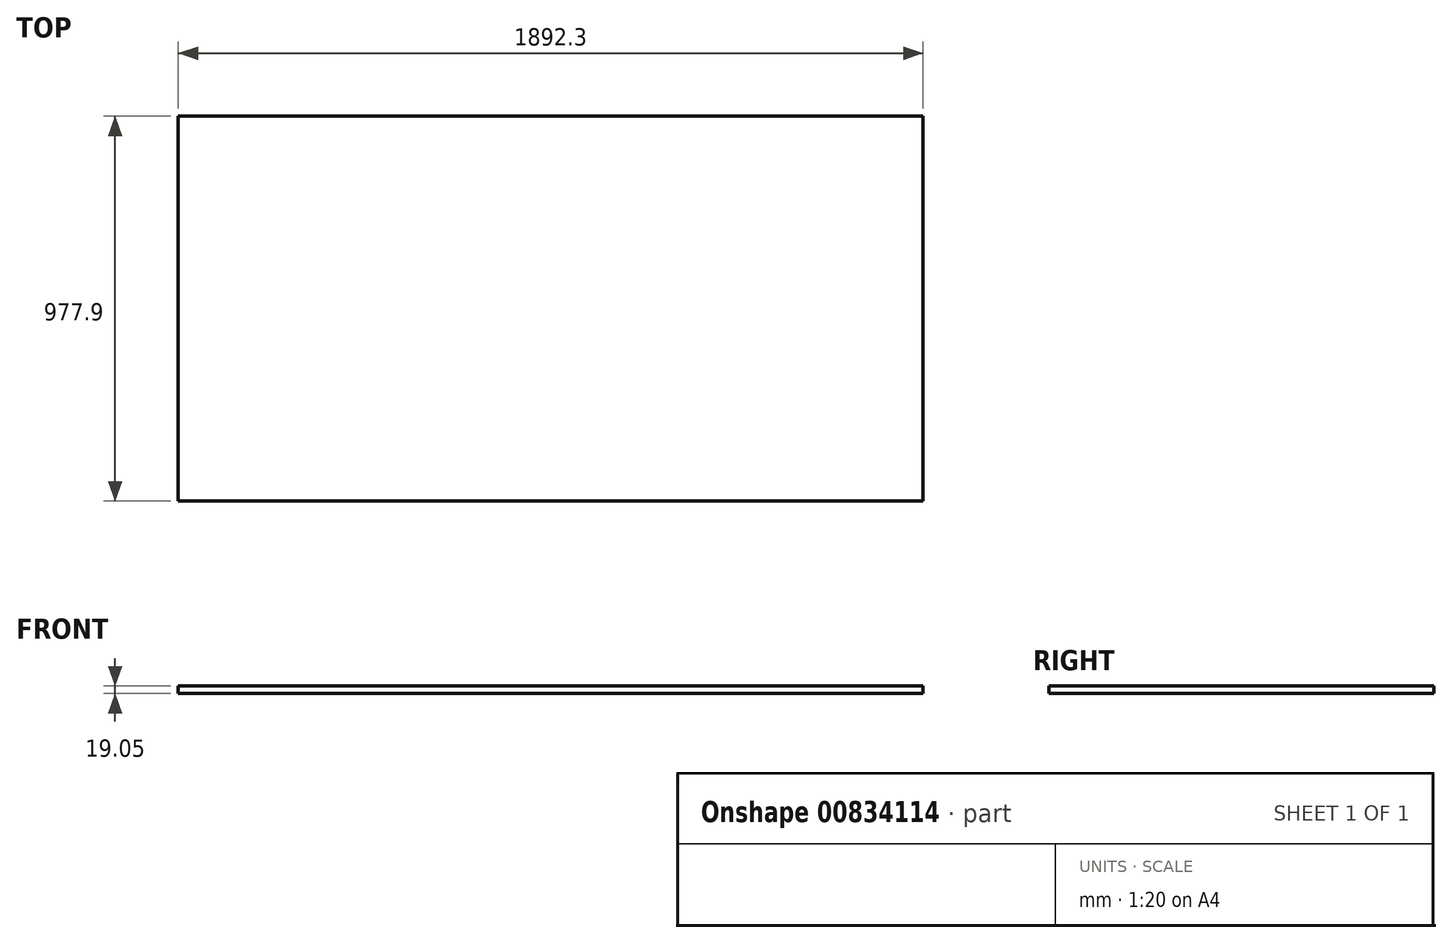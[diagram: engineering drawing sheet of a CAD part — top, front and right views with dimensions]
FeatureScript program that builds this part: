
annotation { "Feature Type Name" : "Feature", "Feature Type Description" : "" }
export const myFeature = defineFeature(function(context is Context, id is Id, definition is map)
    precondition{}
    {
        {
            var Q0;
            Q0=qCreatedBy(makeId("Top.planeOp"),FACE);
            var sketch = newSketch(context, id + "F0", { "sketchPlane" : qUnion([Q0])});
            skLineSegment(sketch, "E0.bottom", {"start": v(946.15, -488.95) * mm, "end": v(-946.15, -488.95) * mm});
            skLineSegment(sketch, "E0.top", {"start": v(946.15, 488.95) * mm, "end": v(-946.15, 488.95) * mm});
            skLineSegment(sketch, "E0.left", {"start": v(946.15, -488.95) * mm, "end": v(946.15, 488.95) * mm});
            skLineSegment(sketch, "E0.right", {"start": v(-946.15, -488.95) * mm, "end": v(-946.15, 488.95) * mm});
            skPoint(sketch, "E0.middle", {"position": v(0, 0) * mm});
            skSolve(sketch);
        }
        {
            var Q0;
            Q0=qSketchRegion(id+"F0",true);
            extrude(context, id + "F1", {"entities" : qUnion([Q0]), "depth" : 19.05 * mm});
        }
    });
